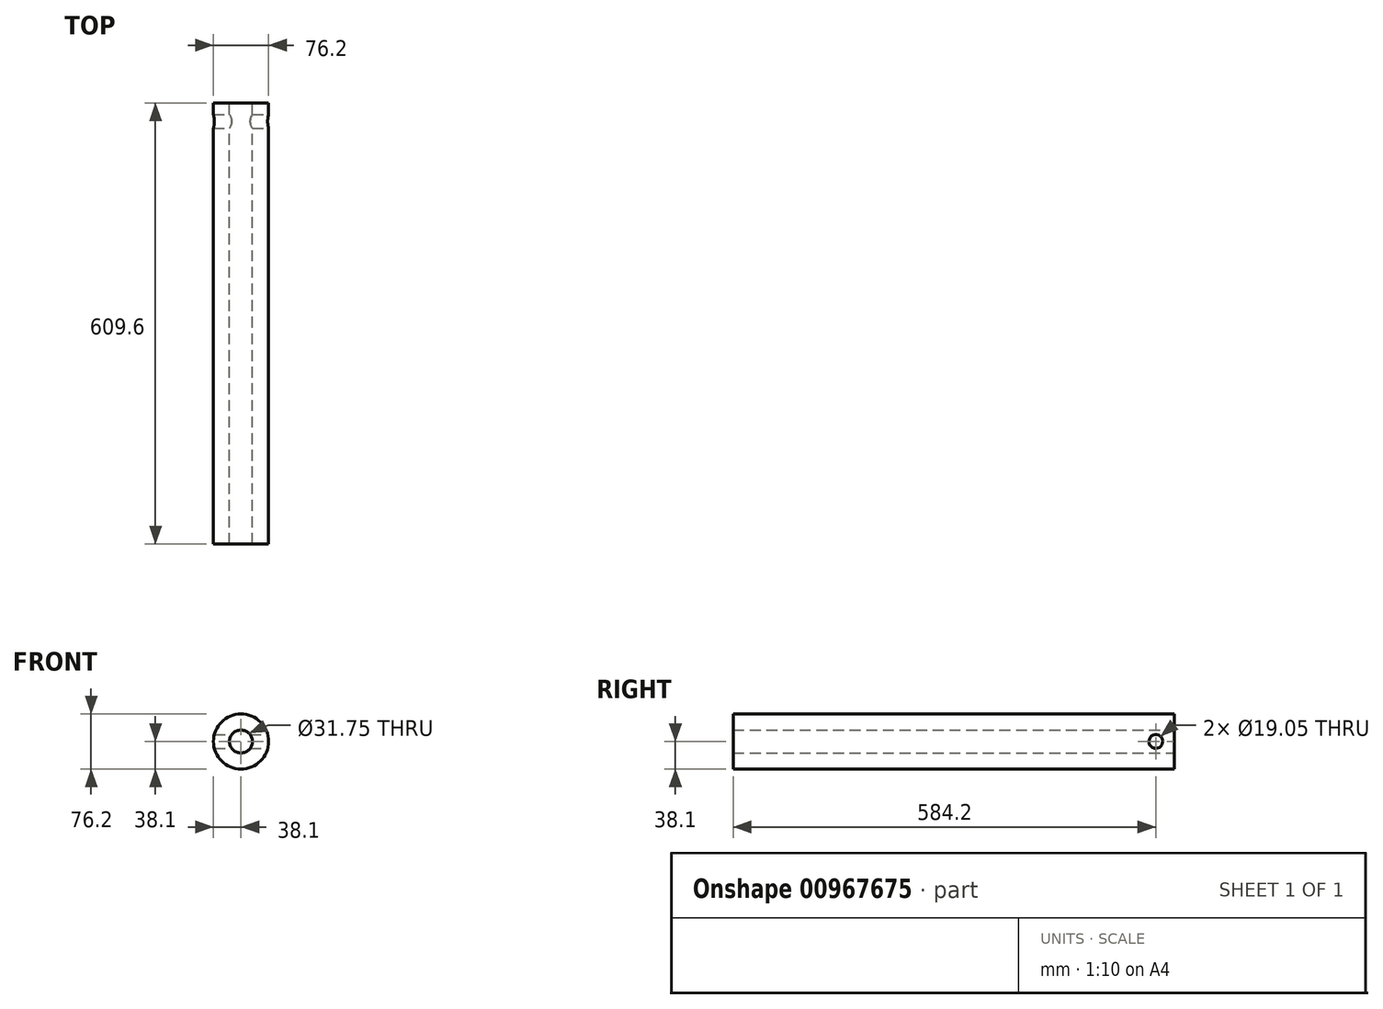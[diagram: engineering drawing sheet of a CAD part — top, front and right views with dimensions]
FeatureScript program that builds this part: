
annotation { "Feature Type Name" : "Feature", "Feature Type Description" : "" }
export const myFeature = defineFeature(function(context is Context, id is Id, definition is map)
    precondition{}
    {
        {
            var Q0;
            Q0=qCreatedBy(makeId("Front.planeOp"),FACE);
            var sketch = newSketch(context, id + "F0", { "sketchPlane" : qUnion([Q0])});
            skCircle(sketch, "E0", {"center": v(0, 0) * mm, "radius": 38.1 * mm});
            skSolve(sketch);
        }
        {
            var Q0;
            Q0 = qSketchRegion(id + "F0", true);
            extrude(context, id + "F1", {"entities" : qUnion([Q0]), "depth" : 609.6 * mm, "offsetDistance" : 25.4 * mm});
        }
        {
            var Q0;
            Q0=qCreatedBy(makeId("Right.planeOp"),FACE);
            var sketch = newSketch(context, id + "F2", { "sketchPlane" : qUnion([Q0])});
            skCircle(sketch, "E1", {"center": v(-25.4, 0) * mm, "radius": 9.53 * mm});
            skSolve(sketch);
        }
        {
            var Q0;
            Q0 = qSketchRegion(id + "F2", true);
            extrude(context, id + "F3", {"entities" : qUnion([Q0]), "operationType" : NewBodyOperationType.REMOVE, "endBound" : BoundingType.THROUGH_ALL, "oppositeDirection" : true, "depth" : 25.4 * mm, "offsetDistance" : 25.4 * mm, "hasSecondDirection" : true, "secondDirectionBound" : BoundingType.THROUGH_ALL, "secondDirectionOppositeDirection" : false, "secondDirectionDepth" : 25.4 * mm});
        }
        {
            var Q0;
            Q0=qCreatedBy(makeId("Front.planeOp"),FACE);
            var sketch = newSketch(context, id + "F4", { "sketchPlane" : qUnion([Q0])});
            skCircle(sketch, "E2", {"center": v(0, 0) * mm, "radius": 15.88 * mm});
            skSolve(sketch);
        }
        {
            var Q0;
            Q0 = qSketchRegion(id + "F4", true);
            extrude(context, id + "F5", {"entities" : qUnion([Q0]), "operationType" : NewBodyOperationType.REMOVE, "endBound" : BoundingType.THROUGH_ALL, "depth" : 25.4 * mm, "offsetDistance" : 25.4 * mm});
        }
    });
